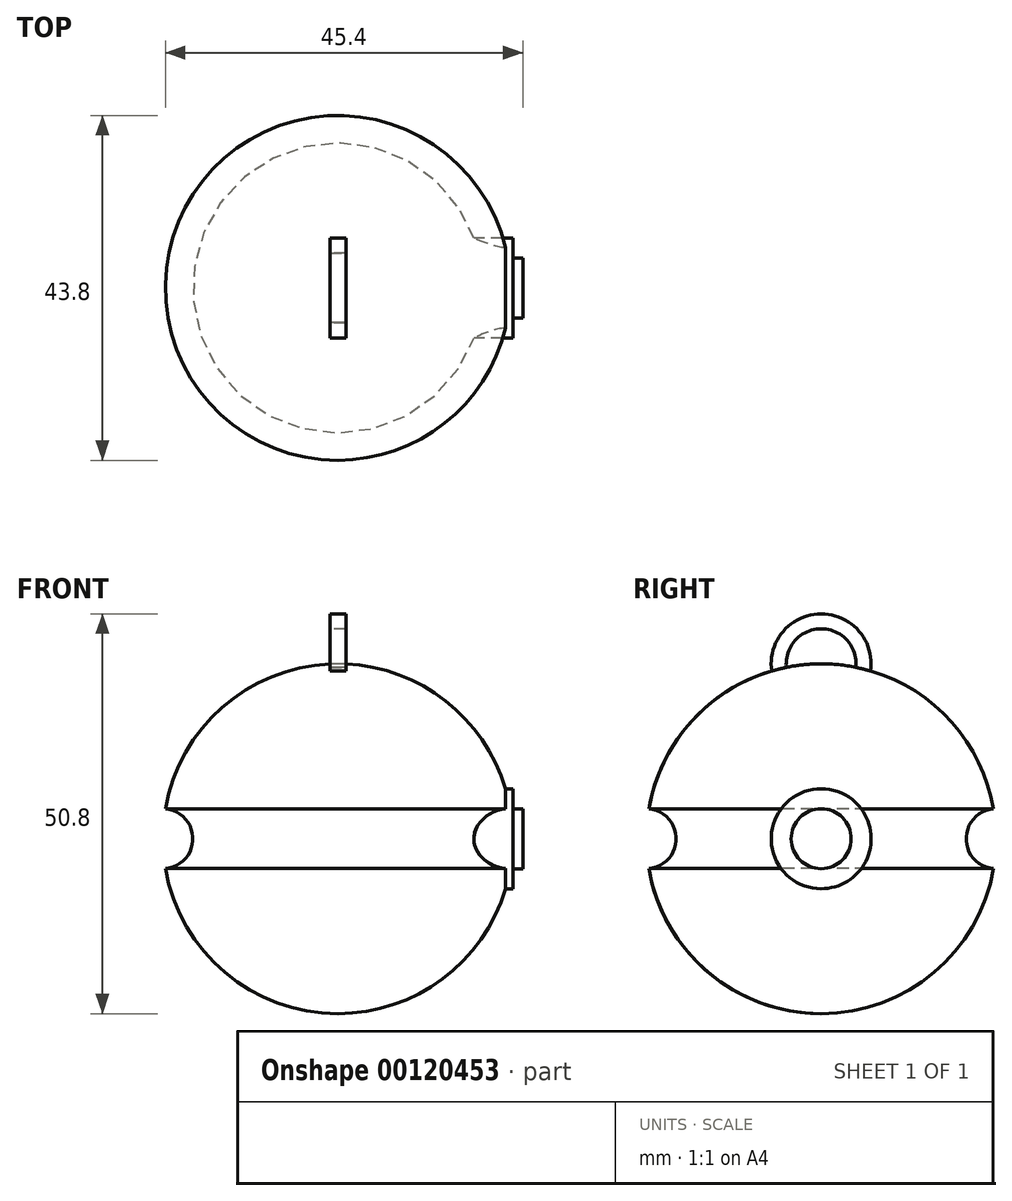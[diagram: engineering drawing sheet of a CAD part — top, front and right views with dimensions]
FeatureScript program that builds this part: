
annotation { "Feature Type Name" : "Feature", "Feature Type Description" : "" }
export const myFeature = defineFeature(function(context is Context, id is Id, definition is map)
    precondition{}
    {
        {
            var Q0;
            Q0=qCreatedBy(makeId("Right.planeOp"),FACE);
            var sketch = newSketch(context, id + "F0", { "sketchPlane" : qUnion([Q0])});
            skArc(sketch, "E0", {"start": v(-21.9, -3.8) * mm, "mid": v(-14.31, -17) * mm, "end": v(0, -22.23) * mm});
            skLineSegment(sketch, "E1", {"start": v(0, 24.56) * mm, "end": v(0, -29.04) * mm});
            skArc(sketch, "E2", {"start": v(-21.9, -3.8) * mm, "mid": v(-18.41, 0) * mm, "end": v(-21.9, 3.8) * mm});
            skArc(sketch, "E3.trimOffspring", {"start": v(0, 22.23) * mm, "mid": v(-14.31, 17) * mm, "end": v(-21.9, 3.8) * mm});
            skSolve(sketch);
        }
        {
            var Q0;
            {var subQ0=sQuery(id+"F0.wireOp",EDGE,"E0");Q0=makeQuery(id+"F0.imprint","IMPRINT",FACE,{"disambiguationData":[TD([[makeQuery(id+"F0.imprint","IMPRINT",EDGE,{"derivedFrom":subQ0}),1.0]])]});}
            var Q1;
            Q1=sQuery(id+"F0.wireOp",EDGE,"E1");
            revolve(context, id + "F1", {"entities" : qUnion([Q0]), "axis" : qUnion([Q1]), "revolveType" : RevolveType.FULL});
        }
        {
            var Q0;
            Q0=qCreatedBy(makeId("Right.planeOp"),FACE);
            var sketch = newSketch(context, id + "F2", { "sketchPlane" : qUnion([Q0])});
            skCircle(sketch, "E4", {"center": v(0, 0) * mm, "radius": 6.35 * mm});
            skSolve(sketch);
        }
        {
            var Q0;
            Q0 = qSketchRegion(id + "F2", true);
            var Q1;
            Q1=sQuery(id+"F2.wireOp",EDGE,"E4");
            extrude(context, id + "F3", {"entities" : qUnion([Q0]), "operationType" : NewBodyOperationType.ADD, "surfaceEntities" : qUnion([Q1]), "depth" : 22.22 * mm});
        }
        {
            var Q0;
            Q0=makeQuery(id+"F3.opExtrude","CAP_FACE",FACE,{"disambiguationData":[OSD([sQuery(id+"F2.wireOp",EDGE,"E4")])],"isStart":false});
            var sketch = newSketch(context, id + "F4", { "sketchPlane" : qUnion([Q0])});
            skCircle(sketch, "E5", {"center": v(0, 0) * mm, "radius": 3.81 * mm});
            skSolve(sketch);
        }
        {
            var Q0;
            Q0 = qSketchRegion(id + "F4", true);
            extrude(context, id + "F5", {"entities" : qUnion([Q0]), "operationType" : NewBodyOperationType.ADD, "depth" : 1.27 * mm});
        }
        {
            var Q0;
            Q0=qCreatedBy(makeId("Right.planeOp"),FACE);
            var sketch = newSketch(context, id + "F6", { "sketchPlane" : qUnion([Q0])});
            skArc(sketch, "E6", {"start": v(6.28, 21.32) * mm, "mid": v(5.36, 21.57) * mm, "end": v(4.42, 21.78) * mm});
            skArc(sketch, "E7.trimOffspring", {"start": v(-4.42, 21.78) * mm, "mid": v(-5.36, 21.57) * mm, "end": v(-6.28, 21.32) * mm});
            skLineSegment(sketch, "E8", {"start": v(0, 28.58) * mm, "end": v(0, 26.67) * mm});
            skCircle(sketch, "E9.converted", {"center": v(0, 22.23) * mm, "radius": 6.35 * mm});
            skCircle(sketch, "E10.converted", {"center": v(0, 22.23) * mm, "radius": 4.45 * mm});
            skLineSegment(sketch, "E11.trimOffspring", {"start": v(0, 17.78) * mm, "end": v(0, 0) * mm});
            skSolve(sketch);
        }
        {
            var Q0;
            {var subQ0=sQuery(id+"F6.wireOp",EDGE,"E6");Q0=makeQuery(id+"F6.imprint","IMPRINT",FACE,{"disambiguationData":[TD([[makeQuery(id+"F6.imprint","IMPRINT",EDGE,{"derivedFrom":subQ0}),-1.0]])]});}
            var Q1;
            {var subQ0=sQuery(id+"F6.wireOp",EDGE,"E6");Q1=makeQuery(id+"F6.imprint","IMPRINT",FACE,{"disambiguationData":[TD([[makeQuery(id+"F6.imprint","IMPRINT",EDGE,{"derivedFrom":subQ0}),1.0]])]});}
            var Q2;
            {var subQ0=sQuery(id+"F6.wireOp",EDGE,"E7.trimOffspring");Q2=makeQuery(id+"F6.imprint","IMPRINT",FACE,{"disambiguationData":[TD([[makeQuery(id+"F6.imprint","IMPRINT",EDGE,{"derivedFrom":subQ0}),1.0]])]});}
            var Q3;
            {var subQ0=sQuery(id+"F6.wireOp",EDGE,"E7.trimOffspring");Q3=makeQuery(id+"F6.imprint","IMPRINT",FACE,{"disambiguationData":[TD([[makeQuery(id+"F6.imprint","IMPRINT",EDGE,{"derivedFrom":subQ0}),-1.0]])]});}
            extrude(context, id + "F7", {"entities" : qUnion([Q0, Q1, Q2, Q3]), "operationType" : NewBodyOperationType.ADD, "endBound" : BoundingType.SYMMETRIC, "depth" : 2.03 * mm});
        }
    });
